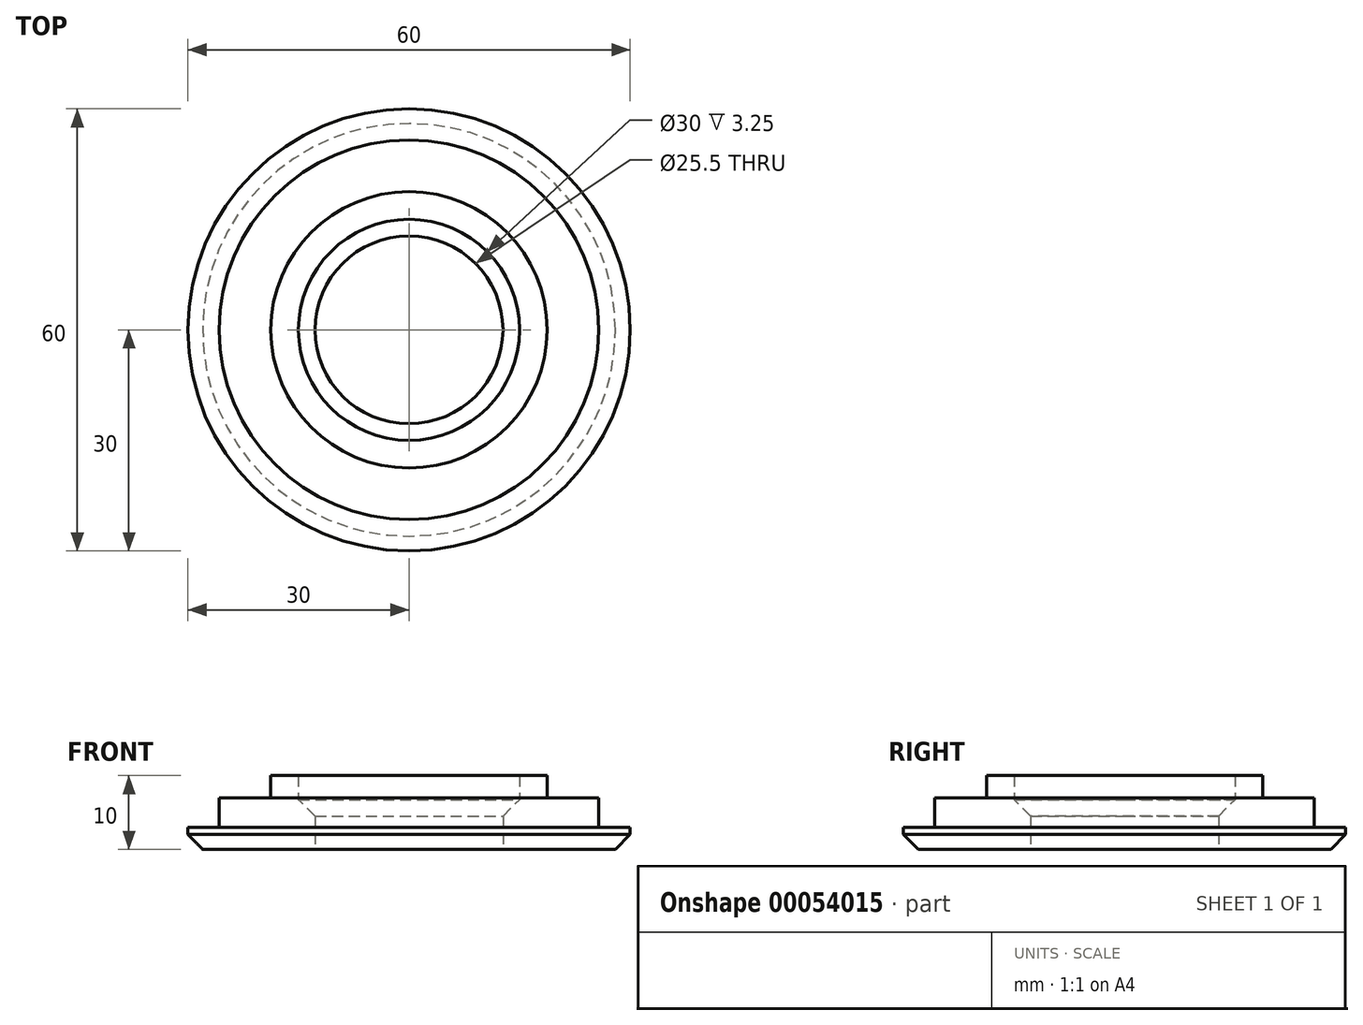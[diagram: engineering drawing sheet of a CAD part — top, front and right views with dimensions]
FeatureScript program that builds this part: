
annotation { "Feature Type Name" : "Feature", "Feature Type Description" : "" }
export const myFeature = defineFeature(function(context is Context, id is Id, definition is map)
    precondition{}
    {
        {
            var Q0;
            Q0=qCreatedBy(makeId("Front.planeOp"),FACE);
            var sketch = newSketch(context, id + "F0", { "sketchPlane" : qUnion([Q0])});
            skLineSegment(sketch, "E0", {"start": v(15, 10) * mm, "end": v(15, 6.75) * mm});
            skLineSegment(sketch, "E1", {"start": v(12.75, 4.5) * mm, "end": v(15, 6.75) * mm});
            skLineSegment(sketch, "E2", {"start": v(12.75, 4.5) * mm, "end": v(12.75, 0) * mm});
            skLineSegment(sketch, "E3", {"start": v(12.75, 0) * mm, "end": v(30, 0) * mm});
            skLineSegment(sketch, "E4", {"start": v(30, 0) * mm, "end": v(30, 3) * mm});
            skLineSegment(sketch, "E5", {"start": v(30, 3) * mm, "end": v(25.75, 3) * mm});
            skLineSegment(sketch, "E6", {"start": v(25.75, 3) * mm, "end": v(25.75, 7) * mm});
            skLineSegment(sketch, "E7", {"start": v(0, 0) * mm, "end": v(0, 21.73) * mm, "construction": true});
            skLineSegment(sketch, "E8", {"start": v(25.75, 7) * mm, "end": v(18.75, 7) * mm});
            skLineSegment(sketch, "E9", {"start": v(18.75, 7) * mm, "end": v(18.75, 10) * mm});
            skLineSegment(sketch, "E10", {"start": v(18.75, 10) * mm, "end": v(15, 10) * mm});
            skSolve(sketch);
        }
        {
            var Q0;
            Q0 = qSketchRegion(id + "F0", true);
            var Q1;
            Q1=sQuery(id+"F0.wireOp",EDGE,"E7");
            revolve(context, id + "F1", {"entities" : qUnion([Q0]), "axis" : qUnion([Q1]), "revolveType" : RevolveType.FULL});
        }
        {
            var Q0;
            Q0=makeQuery(id+"F1.opRevolve","SWEPT_EDGE",EDGE,{"disambiguationData":[OSD([sQuery(id+"F0.wireOp",EDGE,"E3"),sQuery(id+"F0.wireOp",EDGE,"E4")])]});
            chamfer(context, id + "F2", {"entities" : qUnion([Q0]), "width" : 2 * mm, "tangentPropagation" : true});
        }
    });
